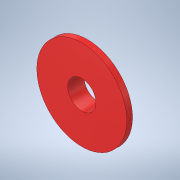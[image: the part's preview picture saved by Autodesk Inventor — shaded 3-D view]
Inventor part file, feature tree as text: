
AUTODESK INVENTOR PART (.ipt)
format: ipt  version: 2021 (Build 250183000, 183)  size: 114,176 bytes
history: native  units: in
note: dims shown in document units (in); Inventor stores cm internally (conversion verified against a paired STEP export)
features: sketch x2, revolve x1, extrude x1
ambient origin geometry x8: Origin, YZ Plane, XZ Plane, XY Plane, X Axis, Y Axis, Z Axis, Center Point
bodies: Solid1 (feature_tree)
feature tree (4):
  revolve  "Revolution1"  [1 undecoded]
  extrude  "Extrusion1"  Depth=0.148in
  sketch  "Sketch1"  dims[d0=0.625in d1=0.0787in]
  sketch  "Sketch2"  dims[d2=0.315in d3=0.148in d4=90.0deg d5=0.394in d6=1.0in d7=0.0in]
note: 1 required parameter value undecoded (feature->parameter linkage not recoverable at this tier; creation-order binding heuristic only, values carry confidence <= 0.55)
